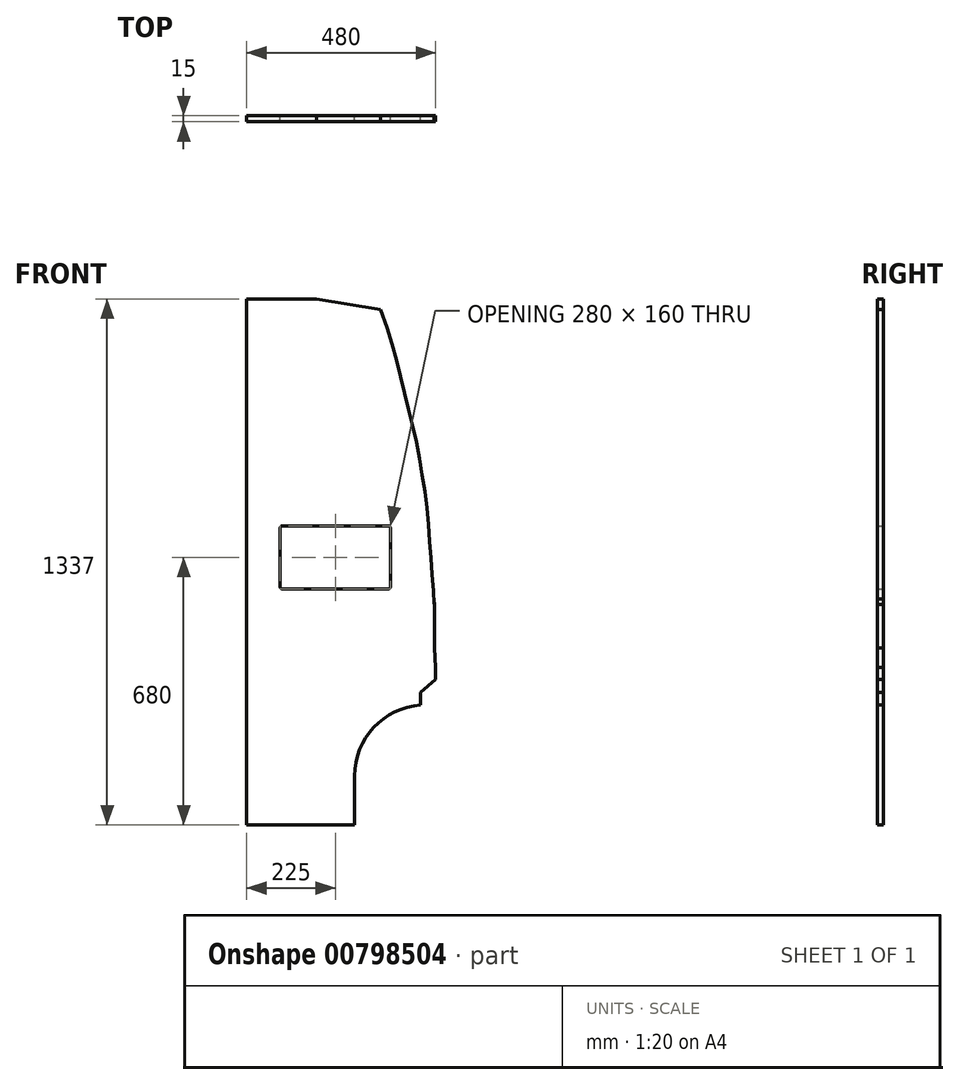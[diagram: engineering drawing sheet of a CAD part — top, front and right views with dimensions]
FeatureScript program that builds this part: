
annotation { "Feature Type Name" : "Feature", "Feature Type Description" : "" }
export const myFeature = defineFeature(function(context is Context, id is Id, definition is map)
    precondition{}
    {
        {
            var Q0;
            Q0=qCreatedBy(makeId("Front.planeOp"),FACE);
            var sketch = newSketch(context, id + "F0", { "sketchPlane" : qUnion([Q0])});
            skLineSegment(sketch, "E0", {"start": v(0, 0) * mm, "end": v(0, -1337) * mm});
            skLineSegment(sketch, "E1", {"start": v(0, -1337) * mm, "end": v(274, -1337) * mm});
            skLineSegment(sketch, "E2", {"start": v(480, -937) * mm, "end": v(480, -967) * mm});
            skLineSegment(sketch, "E3", {"start": v(480, -967) * mm, "end": v(442, -1000) * mm});
            skLineSegment(sketch, "E4", {"start": v(442, -1000) * mm, "end": v(442, -1032) * mm});
            skLineSegment(sketch, "E5", {"start": v(274, -1337) * mm, "end": v(274, -1212) * mm});
            skArc(sketch, "E6", {"start": v(442, -1032) * mm, "mid": v(322.53, -1088.9) * mm, "end": v(274, -1212) * mm});
            skLineSegment(sketch, "E7", {"start": v(480, -937) * mm, "end": v(477, -887) * mm});
            skLineSegment(sketch, "E8", {"start": v(0, 0) * mm, "end": v(177, 0) * mm});
            skLineSegment(sketch, "E9", {"start": v(177, 0) * mm, "end": v(340, -27) * mm});
            skFitSpline(sketch, "E10", {"points": [v(477, -887) * mm, v(477, -837) * mm, v(476.31, -762) * mm, v(476.3, -776.56) * mm, v(474, -737) * mm, v(466, -637) * mm, v(459, -537) * mm, v(444, -437) * mm, v(425, -337) * mm, v(400, -237) * mm, v(375, -137) * mm, v(340, -27) * mm], "startDerivative": vector(14.04, 877.44) * mm, "endDerivative": vector(-418.88, 1141.7) * mm});
            skLineSegment(sketch, "E11.bottom", {"start": v(90, -577) * mm, "end": v(360, -577) * mm});
            skLineSegment(sketch, "E11.top", {"start": v(90, -737) * mm, "end": v(360, -737) * mm});
            skLineSegment(sketch, "E11.left", {"start": v(85, -582) * mm, "end": v(85, -732) * mm});
            skLineSegment(sketch, "E11.right", {"start": v(365, -582) * mm, "end": v(365, -732) * mm});
            skPoint(sketch, "E12.visualSharp", {"position": v(85, -577) * mm});
            skArc(sketch, "E12.filletArc", {"start": v(90, -577) * mm, "mid": v(86.46, -578.46) * mm, "end": v(85, -582) * mm});
            skPoint(sketch, "E13.visualSharp", {"position": v(85, -737) * mm});
            skArc(sketch, "E13.filletArc", {"start": v(85, -732) * mm, "mid": v(86.46, -735.54) * mm, "end": v(90, -737) * mm});
            skPoint(sketch, "E14.visualSharp", {"position": v(365, -737) * mm});
            skArc(sketch, "E14.filletArc", {"start": v(360, -737) * mm, "mid": v(363.54, -735.54) * mm, "end": v(365, -732) * mm});
            skPoint(sketch, "E15.visualSharp", {"position": v(365, -577) * mm});
            skArc(sketch, "E15.filletArc", {"start": v(365, -582) * mm, "mid": v(363.54, -578.46) * mm, "end": v(360, -577) * mm});
            skSolve(sketch);
        }
        {
            var Q0;
            Q0=makeQuery(id+"F0.imprint","IMPRINT",FACE,{"disambiguationData":[TD([[makeQuery(id+"F0.imprint","IMPRINT",EDGE,{"derivedFrom":sQuery(id+"F0.wireOp",EDGE,"E0")}),1.0]])]});
            extrude(context, id + "F1", {"entities" : qUnion([Q0]), "depth" : 15 * mm, "offsetDistance" : 25 * mm});
        }
    });
